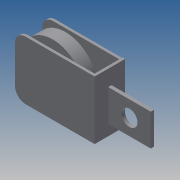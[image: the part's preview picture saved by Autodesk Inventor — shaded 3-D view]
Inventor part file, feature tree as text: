
AUTODESK INVENTOR PART (.ipt)
format: ipt  version: 2013 SP2 (Build 170200200, 200)  size: 135,680 bytes
history: native  units: in
note: dims shown in document units (in); Inventor stores cm internally (conversion verified against a paired STEP export)
features: extrude x6, sketch x6, plane x1, mirror x1
ambient origin geometry x8: Origin, YZ Plane, XZ Plane, XY Plane, X Axis, Y Axis, Z Axis, Center Point
bodies: Solid1 (feature_tree)
feature tree (14):
  extrude  "wheel"  Depth=0.3in TaperAngle=0.0deg
  extrude  "axle"  Depth=0.2in TaperAngle=0.0deg
  extrude  "side"  Depth=0.25in
  plane  "Work Plane1"
  mirror  "Mirror1"
  extrude  "Extrusion4"  Depth=0.06in TaperAngle=0.0deg
  extrude  "Extrusion5"  Depth=0.5in
  extrude  "Extrusion6"  [1 undecoded]
  sketch  "Sketch1"  dims[d0=1.5in d2=0.3in d3=0.0in]
  sketch  "Sketch2"  dims[d4=0.3in d7=0.2in d8=0.5in d9=0.0in d10=0.0in]
  sketch  "Sketch3"  dims[d11=0.06in d12=0.0in d13=0.25in]
  sketch  "Sketch4"  dims[d14=-0.35in d15=0.06in d16=0.0in]
  sketch  "Sketch5"  dims[d17=1.0in d18=0.0in d19=0.5in]
  sketch  "Sketch6"  dims[d20=1.0in d21=0.0in]
note: 1 required parameter value undecoded (feature->parameter linkage not recoverable at this tier; creation-order binding heuristic only, values carry confidence <= 0.55)
